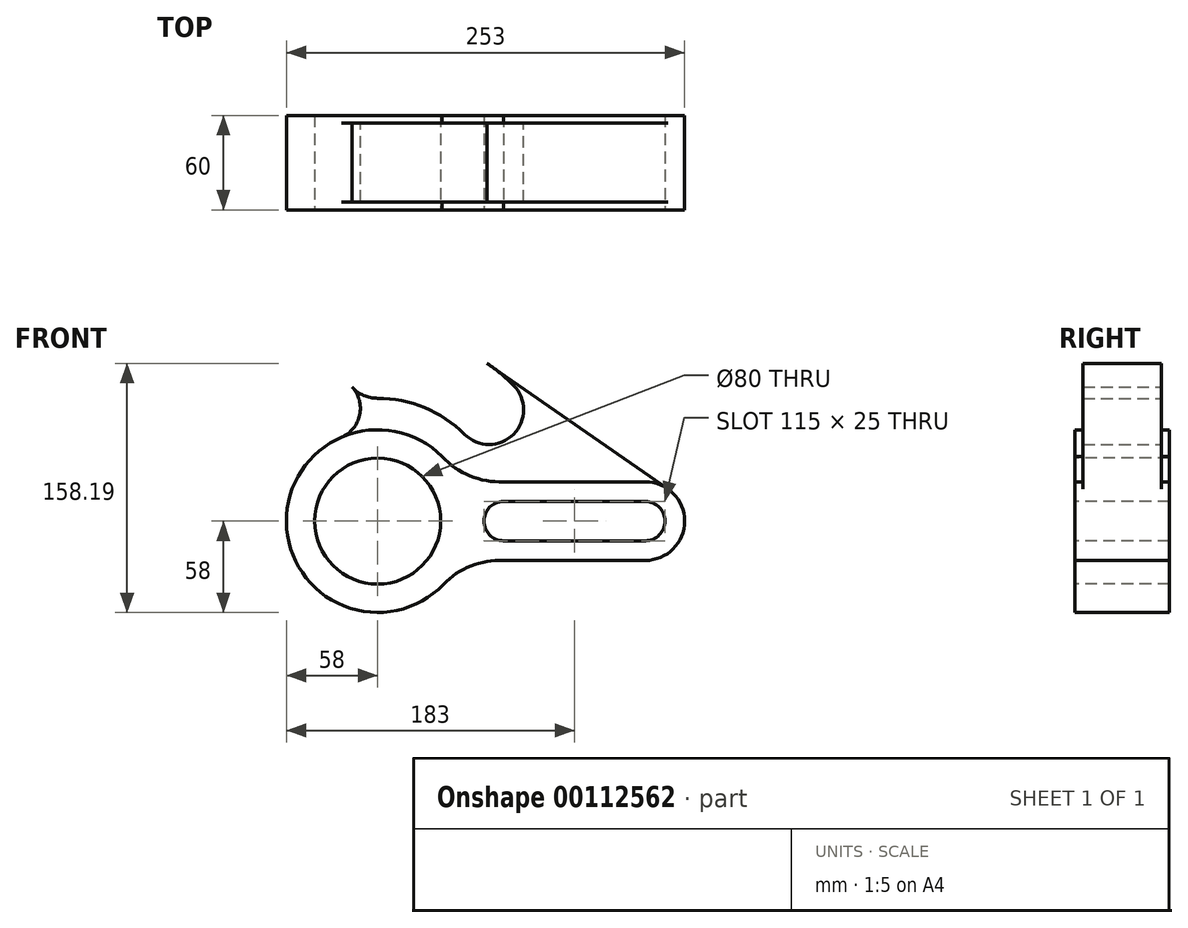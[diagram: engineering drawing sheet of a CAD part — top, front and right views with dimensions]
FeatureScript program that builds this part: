
annotation { "Feature Type Name" : "Feature", "Feature Type Description" : "" }
export const myFeature = defineFeature(function(context is Context, id is Id, definition is map)
    precondition{}
    {
        {
            var Q0;
            Q0=qCreatedBy(makeId("Front.planeOp"),FACE);
            var sketch = newSketch(context, id + "F0", { "sketchPlane" : qUnion([Q0])});
            skCircle(sketch, "E0", {"center": v(0, 0) * mm, "radius": 40 * mm});
            skArc(sketch, "E1", {"start": v(41.01, 41.01) * mm, "mid": v(-58, -0.53) * mm, "end": v(41.76, -40.25) * mm});
            skArc(sketch, "E2", {"start": v(80, 12.5) * mm, "mid": v(67.5, 0) * mm, "end": v(80, -12.5) * mm});
            skArc(sketch, "E3", {"start": v(170, -12.5) * mm, "mid": v(182.5, 0) * mm, "end": v(170, 12.5) * mm});
            skLineSegment(sketch, "E4", {"start": v(80, 12.5) * mm, "end": v(170, 12.5) * mm});
            skLineSegment(sketch, "E5", {"start": v(80, -12.5) * mm, "end": v(170, -12.5) * mm});
            skArc(sketch, "E6", {"start": v(170, -25) * mm, "mid": v(195, 0) * mm, "end": v(170, 25) * mm});
            skLineSegment(sketch, "E7", {"start": v(170, 25) * mm, "end": v(80, 25) * mm});
            skLineSegment(sketch, "E8", {"start": v(170, -25) * mm, "end": v(80, -25) * mm});
            skPoint(sketch, "E9.visualSharp", {"position": v(80, -25) * mm});
            skLineSegment(sketch, "E10", {"start": v(0, 0) * mm, "end": v(154, 154) * mm, "construction": true});
            skLineSegment(sketch, "E11", {"start": v(0, 100) * mm, "end": v(0, 0) * mm, "construction": true});
            skArc(sketch, "E12", {"start": v(70.71, 70.71) * mm, "mid": v(38.27, 92.39) * mm, "end": v(0, 100) * mm, "construction": true});
            skArc(sketch, "E13.0.startCap", {"start": v(86.27, 86.27) * mm, "mid": v(86.27, 55.15) * mm, "end": v(55.15, 55.15) * mm});
            skArc(sketch, "E13.0.endCap", {"start": v(0, 78) * mm, "mid": v(-22, 100) * mm, "end": v(0, 122) * mm});
            skArc(sketch, "E13.0.left", {"start": v(55.15, 55.15) * mm, "mid": v(29.85, 72.06) * mm, "end": v(0, 78) * mm});
            skArc(sketch, "E13.0.right", {"start": v(86.27, 86.27) * mm, "mid": v(46.69, 112.71) * mm, "end": v(0, 122) * mm});
            skArc(sketch, "E14.0", {"start": v(77.07, 77.07) * mm, "mid": v(41.71, 100.7) * mm, "end": v(0, 109) * mm});
            skArc(sketch, "E14.1", {"start": v(77.07, 77.07) * mm, "mid": v(77.07, 64.35) * mm, "end": v(64.35, 64.35) * mm});
            skArc(sketch, "E14.2", {"start": v(64.35, 64.35) * mm, "mid": v(34.82, 84.07) * mm, "end": v(0, 91) * mm});
            skArc(sketch, "E14.3", {"start": v(0, 91) * mm, "mid": v(-9, 100) * mm, "end": v(0, 109) * mm});
            skLineSegment(sketch, "E15", {"start": v(69.61, 100.2) * mm, "end": v(184.26, 20.53) * mm});
            skArc(sketch, "E16", {"start": v(-23, 53.24) * mm, "mid": v(-11.38, 67.43) * mm, "end": v(-16.2, 85.12) * mm});
            skArc(sketch, "E17", {"start": v(41.76, -40.25) * mm, "mid": v(59.24, -28.5) * mm, "end": v(80, -25) * mm});
            skArc(sketch, "E18", {"start": v(41.01, 41.01) * mm, "mid": v(58.74, 28.7) * mm, "end": v(80, 25) * mm});
            skSolve(sketch);
        }
        {
            var Q0;
            Q0=makeQuery(id+"F0.imprint","IMPRINT",FACE,{"disambiguationData":[TD([[makeQuery(id+"F0.imprint","IMPRINT",EDGE,{"derivedFrom":sQuery(id+"F0.wireOp",EDGE,"E0")}),-1.0]])]});
            extrude(context, id + "F1", {"entities" : qUnion([Q0]), "endBound" : BoundingType.SYMMETRIC, "oppositeDirection" : true, "depth" : 60 * mm});
        }
        {
            var Q0;
            {var subQ1=sQuery(id+"F0.wireOp",EDGE,"E7");Q0=makeQuery(id+"F0.imprint","IMPRINT",FACE,{"disambiguationData":[TD([[makeQuery(id+"F0.imprint","IMPRINT",EDGE,{"derivedFrom":subQ1}),-1.0]])]});}
            extrude(context, id + "F2", {"entities" : qUnion([Q0]), "operationType" : NewBodyOperationType.ADD, "endBound" : BoundingType.SYMMETRIC, "depth" : 30 * mm});
        }
        {
            var Q0;
            {var subQ6=sQuery(id+"F0.wireOp",EDGE,"E13.0.startCap");Q0=makeQuery(id+"F0.imprint","IMPRINT",FACE,{"disambiguationData":[TD([[makeQuery(id+"F0.imprint","IMPRINT",EDGE,{"derivedFrom":subQ6}),-1.0]])]});}
            extrude(context, id + "F3", {"entities" : qUnion([Q0]), "operationType" : NewBodyOperationType.ADD, "endBound" : BoundingType.SYMMETRIC, "depth" : 50 * mm});
        }
    });
